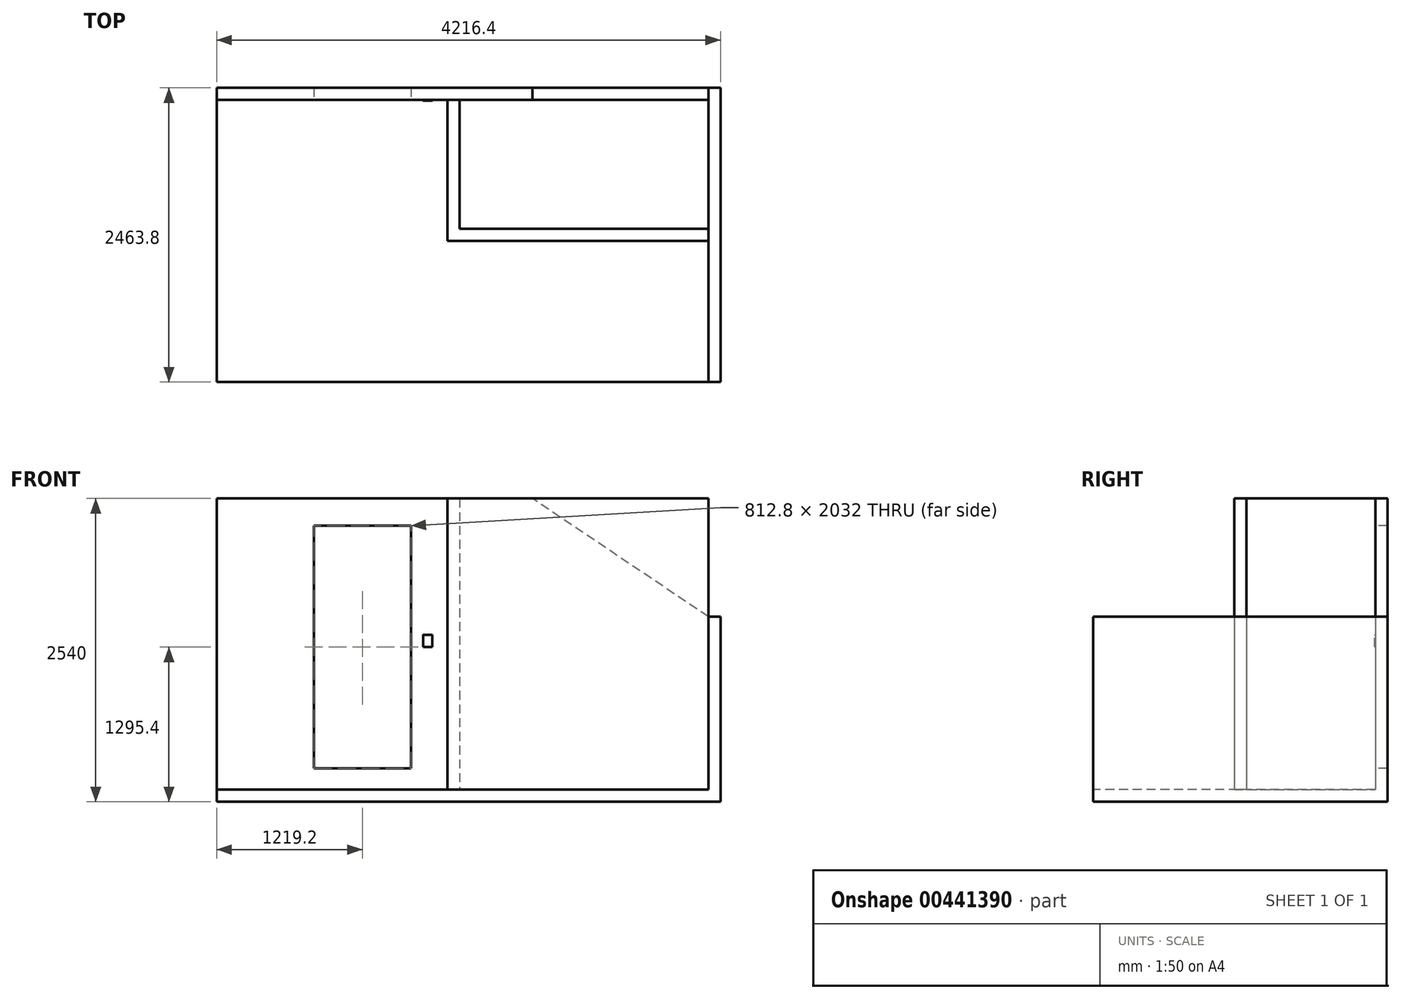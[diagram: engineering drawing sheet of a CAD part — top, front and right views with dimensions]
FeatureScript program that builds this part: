
annotation { "Feature Type Name" : "Feature", "Feature Type Description" : "" }
export const myFeature = defineFeature(function(context is Context, id is Id, definition is map)
    precondition{}
    {
        {
            var Q0;
            Q0=qCreatedBy(makeId("Top.planeOp"),FACE);
            var sketch = newSketch(context, id + "F0", { "sketchPlane" : qUnion([Q0])});
            skLineSegment(sketch, "E0", {"start": v(0, 0) * mm, "end": v(-4114.8, 0) * mm});
            skLineSegment(sketch, "E1", {"start": v(0, 0) * mm, "end": v(0, -2362.2) * mm});
            skLineSegment(sketch, "E2.0", {"start": v(101.6, 101.6) * mm, "end": v(101.6, -2362.2) * mm});
            skLineSegment(sketch, "E3.0", {"start": v(101.6, 101.6) * mm, "end": v(-4114.8, 101.6) * mm});
            skLineSegment(sketch, "E4", {"start": v(0, -2362.2) * mm, "end": v(101.6, -2362.2) * mm});
            skLineSegment(sketch, "E5", {"start": v(-4114.8, 0) * mm, "end": v(-4114.8, 101.6) * mm});
            skSolve(sketch);
        }
        {
            var Q0;
            Q0=makeQuery(id+"F0.imprint","IMPRINT",FACE,{"disambiguationData":[TD([[makeQuery(id+"F0.imprint","IMPRINT",EDGE,{"derivedFrom":sQuery(id+"F0.wireOp",EDGE,"E0")}),-1.0]])]});
            extrude(context, id + "F1", {"entities" : qUnion([Q0]), "depth" : 2438.4 * mm});
        }
        {
            var Q0;
            Q0=makeQuery(id+"F1.opExtrude","SWEPT_FACE",FACE,{"disambiguationData":[OSD([sQuery(id+"F0.wireOp",EDGE,"E0")])]});
            var sketch = newSketch(context, id + "F2", { "sketchPlane" : qUnion([Q0])});
            skLineSegment(sketch, "E6", {"start": v(0, 0) * mm, "end": v(-2489.2, 0) * mm});
            skLineSegment(sketch, "E7", {"start": v(-2489.2, 0) * mm, "end": v(-2489.2, 2209.8) * mm});
            skLineSegment(sketch, "E8", {"start": v(-2489.2, 2209.8) * mm, "end": v(-3302, 2209.8) * mm});
            skLineSegment(sketch, "E9", {"start": v(-3302, 2209.8) * mm, "end": v(-3302, 177.8) * mm});
            skLineSegment(sketch, "E10", {"start": v(-3302, 177.8) * mm, "end": v(-2489.2, 177.8) * mm});
            skLineSegment(sketch, "E11", {"start": v(-2489.2, 0) * mm, "end": v(-1473.2, 0) * mm});
            skLineSegment(sketch, "E12", {"start": v(-1473.2, 0) * mm, "end": v(-1473.2, 2438.4) * mm});
            skLineSegment(sketch, "E13", {"start": v(0, 0) * mm, "end": v(0, 1447.8) * mm});
            skLineSegment(sketch, "E14", {"start": v(0, 1447.8) * mm, "end": v(-1473.2, 2438.4) * mm});
            skLineSegment(sketch, "E15", {"start": v(103.75, 2438.4) * mm, "end": v(103.75, 1447.8) * mm});
            skLineSegment(sketch, "E16", {"start": v(103.75, 1447.8) * mm, "end": v(0, 1447.8) * mm});
            skSolve(sketch);
        }
        {
            var Q0;
            {var subQ0=sQuery(id+"F2.wireOp",EDGE,"E8");Q0=makeQuery(id+"F2.imprint","IMPRINT",FACE,{"disambiguationData":[TD([[makeQuery(id+"F2.imprint","IMPRINT",EDGE,{"derivedFrom":subQ0}),1.0]])]});}
            var Q1;
            {var subQ0=sQuery(id+"F2.wireOp",EDGE,"E14");Q1=makeQuery(id+"F2.imprint","IMPRINT",FACE,{"disambiguationData":[TD([[makeQuery(id+"F2.imprint","IMPRINT",EDGE,{"derivedFrom":subQ0}),-1.0]])]});}
            extrude(context, id + "F3", {"entities" : qUnion([Q0, Q1]), "operationType" : NewBodyOperationType.REMOVE, "endBound" : BoundingType.THROUGH_ALL, "oppositeDirection" : true, "depth" : 25.4 * mm});
        }
        {
            var Q0;
            Q0=makeQuery(id+"F1.opExtrude","SWEPT_FACE",FACE,{"disambiguationData":[OSD([sQuery(id+"F0.wireOp",EDGE,"E2.0")])]});
            var sketch = newSketch(context, id + "F4", { "sketchPlane" : qUnion([Q0])});
            skLineSegment(sketch, "E17", {"start": v(-2362.2, 0) * mm, "end": v(-2362.2, 1447.8) * mm});
            skLineSegment(sketch, "E18", {"start": v(-2362.2, 1447.8) * mm, "end": v(101.6, 1447.8) * mm});
            skLineSegment(sketch, "E19", {"start": v(101.6, 1447.8) * mm, "end": v(101.6, 2438.4) * mm});
            skLineSegment(sketch, "E20", {"start": v(101.6, 2438.4) * mm, "end": v(-2362.2, 2438.4) * mm});
            skLineSegment(sketch, "E21", {"start": v(-2362.2, 2438.4) * mm, "end": v(-2362.2, 1447.8) * mm});
            skSolve(sketch);
        }
        {
            var Q0;
            Q0=makeQuery(id+"F4.imprint","IMPRINT",FACE,{"disambiguationData":[TD([[makeQuery(id+"F4.imprint","IMPRINT",EDGE,{"derivedFrom":sQuery(id+"F4.wireOp",EDGE,"E18")}),1.0]])]});
            extrude(context, id + "F5", {"entities" : qUnion([Q0]), "operationType" : NewBodyOperationType.REMOVE, "oppositeDirection" : true, "depth" : 101.6 * mm});
        }
        {
            var Q0;
            Q0=makeQuery(id+"FdU01Bb6jOvbdIS_1.boolean.opBoolean","MERGE",FACE,{"derivedFrom":[makeQuery(id+"F1.opExtrude","SWEPT_FACE",FACE,{"disambiguationData":[OSD([sQuery(id+"F0.wireOp",EDGE,"E3.0")])]}),makeQuery(id+"FdU01Bb6jOvbdIS_1.opExtrude","CAP_FACE",FACE,{"disambiguationData":[OSD([sQuery(id+"FIBbBVe9nBCGcdl_1.wireOp",EDGE,"07785311-34f3-4b7e-b31d-a8fb6ae8fb2a.0"),sQuery(id+"FIBbBVe9nBCGcdl_1.wireOp",EDGE,"5e91c4da-99d9-494f-a7db-e7e1effcf30b.0"),sQuery(id+"FIBbBVe9nBCGcdl_1.wireOp",EDGE,"cfWalp6H-2e5D-VNrO-PFqi-9NUexkil3CjR"),sQuery(id+"FIBbBVe9nBCGcdl_1.wireOp",EDGE,"ysYQvT0D-cF3q-znkB-RapE-xj1YypymD8X7"),sQuery(id+"FIBbBVe9nBCGcdl_1.wireOp",EDGE,"qJqkscx8-5Ibl-L8JI-gS4E-D0uuXNeZafbp"),sQuery(id+"FIBbBVe9nBCGcdl_1.wireOp",EDGE,"pQMztFvv-7scu-0Ohy-FeIP-zb4BjNBvwknY"),sQuery(id+"FIBbBVe9nBCGcdl_1.wireOp",EDGE,"MKQ2pC5Y-jgYu-aTSN-IoGb-JxwjcmEyPy9W")])],"isStart":true})]});
            var sketch = newSketch(context, id + "F6", { "sketchPlane" : qUnion([Q0])});
            skLineSegment(sketch, "E22", {"start": v(4114.8, 0) * mm, "end": v(-101.6, 0) * mm});
            skLineSegment(sketch, "E23", {"start": v(-101.6, 0) * mm, "end": v(-101.6, -101.6) * mm});
            skLineSegment(sketch, "E24", {"start": v(-101.6, -101.6) * mm, "end": v(4114.8, -101.6) * mm});
            skLineSegment(sketch, "E25", {"start": v(4114.8, -101.6) * mm, "end": v(4114.8, 0) * mm});
            skSolve(sketch);
        }
        {
            var Q0;
            Q0=makeQuery(id+"F6.imprint","IMPRINT",FACE,{"disambiguationData":[TD([[makeQuery(id+"F6.imprint","IMPRINT",EDGE,{"derivedFrom":sQuery(id+"F6.wireOp",EDGE,"E22")}),-1.0]])]});
            extrude(context, id + "F7", {"entities" : qUnion([Q0]), "operationType" : NewBodyOperationType.ADD, "oppositeDirection" : true, "depth" : 2463.8 * mm});
        }
        {
            var Q0;
            Q0=makeQuery(id+"F1.opExtrude","SWEPT_FACE",FACE,{"disambiguationData":[OSD([sQuery(id+"F0.wireOp",EDGE,"E0")])]});
            var sketch = newSketch(context, id + "F8", { "sketchPlane" : qUnion([Q0])});
            skLineSegment(sketch, "E26", {"start": v(-2489.2, 0) * mm, "end": v(-2489.2, 1193.8) * mm});
            skLineSegment(sketch, "E27", {"start": v(-2489.2, 1193.8) * mm, "end": v(-2311.4, 1193.8) * mm});
            skLineSegment(sketch, "E28", {"start": v(-2311.4, 1193.8) * mm, "end": v(-2311.4, 1295.4) * mm});
            skLineSegment(sketch, "E29", {"start": v(-2311.4, 1295.4) * mm, "end": v(-2387.6, 1295.4) * mm});
            skLineSegment(sketch, "E30", {"start": v(-2387.6, 1295.4) * mm, "end": v(-2387.6, 1193.8) * mm});
            skSolve(sketch);
        }
        {
            var Q0;
            {var subQ0=sQuery(id+"F8.wireOp",EDGE,"E28");Q0=makeQuery(id+"F8.imprint","IMPRINT",FACE,{"disambiguationData":[TD([[makeQuery(id+"F8.imprint","IMPRINT",EDGE,{"derivedFrom":subQ0}),1.0]])]});}
            extrude(context, id + "F9", {"entities" : qUnion([Q0]), "operationType" : NewBodyOperationType.ADD, "depth" : 6.35 * mm});
        }
        {
            var Q0;
            Q0=makeQuery(id+"F9.opExtrude","CAP_EDGE",EDGE,{"disambiguationData":[OSD([sQuery(id+"F8.wireOp",EDGE,"E29")])],"isStart":false});
            var Q1;
            Q1=makeQuery(id+"F9.opExtrude","CAP_EDGE",EDGE,{"disambiguationData":[OSD([sQuery(id+"F8.wireOp",EDGE,"E30")])],"isStart":false});
            var Q2;
            Q2=makeQuery(id+"F9.opExtrude","CAP_EDGE",EDGE,{"disambiguationData":[OSD([sQuery(id+"F8.wireOp",EDGE,"E27")])],"isStart":false});
            var Q3;
            Q3=makeQuery(id+"F9.opExtrude","CAP_EDGE",EDGE,{"disambiguationData":[OSD([sQuery(id+"F8.wireOp",EDGE,"E28")])],"isStart":false});
            fillet(context, id + "F10", {"entities" : qUnion([Q0, Q1, Q2, Q3]), "radius" : 2.54 * mm, "tangentPropagation" : true, "allowEdgeOverflow" : false});
        }
        {
            var Q0;
            Q0=makeQuery(id+"F1.opExtrude","SWEPT_FACE",FACE,{"disambiguationData":[OSD([sQuery(id+"F0.wireOp",EDGE,"E0")])]});
            var sketch = newSketch(context, id + "F11", { "sketchPlane" : qUnion([Q0])});
            skLineSegment(sketch, "E31", {"start": v(0, 0) * mm, "end": v(-2209.8, 0) * mm});
            skLineSegment(sketch, "E32", {"start": v(-2209.8, 0) * mm, "end": v(-2209.8, 2438.4) * mm});
            skLineSegment(sketch, "E33", {"start": v(-2209.8, 2438.4) * mm, "end": v(-1473.2, 2438.4) * mm});
            skLineSegment(sketch, "E34", {"start": v(-1473.2, 2438.4) * mm, "end": v(0, 1447.8) * mm});
            skLineSegment(sketch, "E35", {"start": v(0, 1447.8) * mm, "end": v(0, 0) * mm});
            skSolve(sketch);
        }
        {
            var Q0;
            Q0=makeQuery(id+"F11.imprint","IMPRINT",FACE,{"disambiguationData":[TD([[makeQuery(id+"F11.imprint","IMPRINT",EDGE,{"derivedFrom":sQuery(id+"F11.wireOp",EDGE,"E31")}),-1.0]])]});
            extrude(context, id + "F12", {"entities" : qUnion([Q0]), "depth" : 914.4 * mm});
        }
        {
            var Q0;
            Q0=makeQuery(id+"F12.opExtrude","SWEPT_BODY",BODY,{"disambiguationData":[OSD([sQuery(id+"F11.wireOp",EDGE,"E31"),sQuery(id+"F11.wireOp",EDGE,"E32"),sQuery(id+"F11.wireOp",EDGE,"E33"),sQuery(id+"F11.wireOp",EDGE,"E34"),sQuery(id+"F11.wireOp",EDGE,"E35")])]});
            deleteBodies(context, id + "F13", {"entities" : qUnion([Q0])});
        }
        {
            var Q0;
            Q0=makeQuery(id+"F7.opExtrude","SWEPT_FACE",FACE,{"disambiguationData":[OSD([sQuery(id+"F6.wireOp",EDGE,"E22")])]});
            var sketch = newSketch(context, id + "F14", { "sketchPlane" : qUnion([Q0])});
            skLineSegment(sketch, "E36", {"start": v(0, -1181.1) * mm, "end": v(-2184.4, -1181.1) * mm});
            skPoint(sketch, "E36.endSnap0", {"position": v(0, -1181.1) * mm});
            skLineSegment(sketch, "E37", {"start": v(-2184.4, -1181.1) * mm, "end": v(-2184.4, 0) * mm});
            skLineSegment(sketch, "E38.0", {"start": v(-2082.8, -1079.5) * mm, "end": v(-2082.8, 0) * mm});
            skLineSegment(sketch, "E39.0", {"start": v(0, -1079.5) * mm, "end": v(-2082.8, -1079.5) * mm});
            skSolve(sketch);
        }
        {
            var Q0;
            {var subQ3=sQuery(id+"F14.wireOp",EDGE,"E36");Q0=makeQuery(id+"F14.imprint","IMPRINT",FACE,{"disambiguationData":[TD([[makeQuery(id+"F14.imprint","IMPRINT",EDGE,{"derivedFrom":subQ3}),-1.0]])]});}
            extrude(context, id + "F15", {"entities" : qUnion([Q0]), "depth" : 2438.4 * mm});
        }
    });
